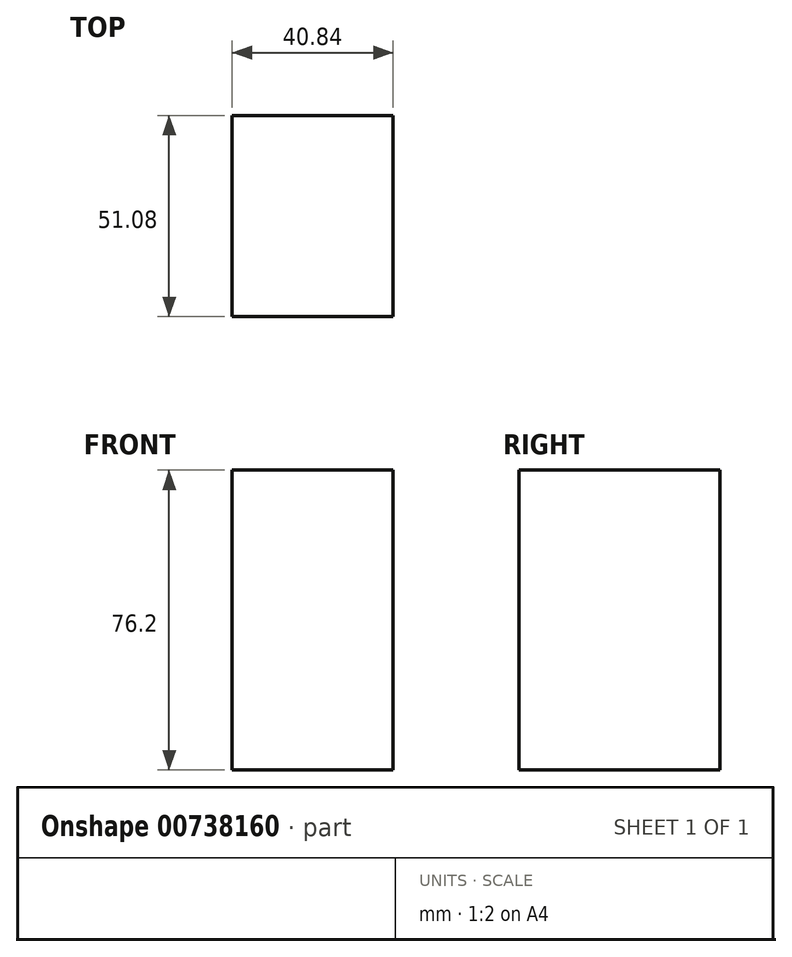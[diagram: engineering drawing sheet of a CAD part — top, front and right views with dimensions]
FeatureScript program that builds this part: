
annotation { "Feature Type Name" : "Feature", "Feature Type Description" : "" }
export const myFeature = defineFeature(function(context is Context, id is Id, definition is map)
    precondition{}
    {
        {
            var Q0;
            Q0=qCreatedBy(makeId("Top.planeOp"),FACE);
            var sketch = newSketch(context, id + "F0", { "sketchPlane" : qUnion([Q0])});
            skLineSegment(sketch, "E0.bottom", {"start": v(20.42, 25.54) * mm, "end": v(-20.42, 25.54) * mm});
            skLineSegment(sketch, "E0.top", {"start": v(20.42, -25.54) * mm, "end": v(-20.42, -25.54) * mm});
            skLineSegment(sketch, "E0.left", {"start": v(20.42, 25.54) * mm, "end": v(20.42, -25.54) * mm});
            skLineSegment(sketch, "E0.right", {"start": v(-20.42, 25.54) * mm, "end": v(-20.42, -25.54) * mm});
            skPoint(sketch, "E0.middle", {"position": v(0, 0) * mm});
            skSolve(sketch);
        }
        {
            var Q0;
            Q0=makeQuery(id+"F0.imprint","IMPRINT",FACE,{"disambiguationData":[TD([[makeQuery(id+"F0.imprint","IMPRINT",EDGE,{"derivedFrom":sQuery(id+"F0.wireOp",EDGE,"E0.bottom")}),1.0]])]});
            extrude(context, id + "F1", {"entities" : qUnion([Q0]), "depth" : 76.2 * mm, "offsetDistance" : 25.4 * mm});
        }
    });
